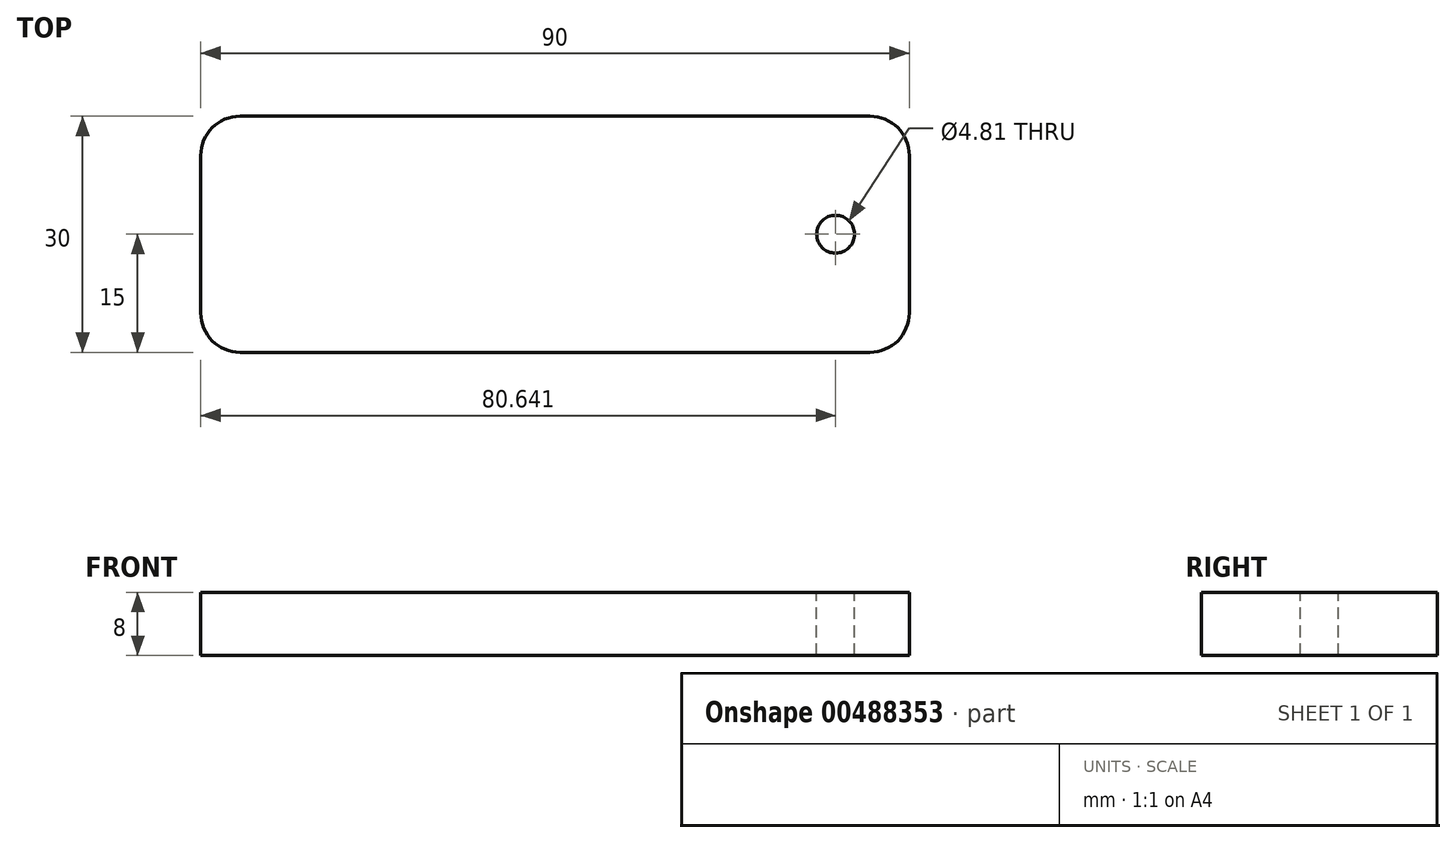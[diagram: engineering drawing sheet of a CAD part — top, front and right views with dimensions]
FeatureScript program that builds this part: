
annotation { "Feature Type Name" : "Feature", "Feature Type Description" : "" }
export const myFeature = defineFeature(function(context is Context, id is Id, definition is map)
    precondition{}
    {
        {
            var Q0;
            Q0=qCreatedBy(makeId("Top.planeOp"),FACE);
            var sketch = newSketch(context, id + "F0", { "sketchPlane" : qUnion([Q0])});
            skLineSegment(sketch, "E0.bottom", {"start": v(40, 15) * mm, "end": v(-40, 15) * mm});
            skLineSegment(sketch, "E0.top", {"start": v(40, -15) * mm, "end": v(-40, -15) * mm});
            skLineSegment(sketch, "E0.left", {"start": v(45, 10) * mm, "end": v(45, -10) * mm});
            skLineSegment(sketch, "E0.right", {"start": v(-45, 10) * mm, "end": v(-45, -10) * mm});
            skPoint(sketch, "E0.middle", {"position": v(0, 0) * mm});
            skPoint(sketch, "E1.visualSharp", {"position": v(-45, 15) * mm});
            skArc(sketch, "E1.filletArc", {"start": v(-40, 15) * mm, "mid": v(-43.54, 13.54) * mm, "end": v(-45, 10) * mm});
            skPoint(sketch, "E2.visualSharp", {"position": v(-45, -15) * mm});
            skArc(sketch, "E2.filletArc", {"start": v(-45, -10) * mm, "mid": v(-43.54, -13.54) * mm, "end": v(-40, -15) * mm});
            skPoint(sketch, "E3.visualSharp", {"position": v(45, 15) * mm});
            skArc(sketch, "E3.filletArc", {"start": v(45, 10) * mm, "mid": v(43.54, 13.54) * mm, "end": v(40, 15) * mm});
            skPoint(sketch, "E4.visualSharp", {"position": v(45, -15) * mm});
            skArc(sketch, "E4.filletArc", {"start": v(40, -15) * mm, "mid": v(43.54, -13.54) * mm, "end": v(45, -10) * mm});
            skSolve(sketch);
        }
        {
            var Q0;
            Q0 = qSketchRegion(id + "F0", true);
            extrude(context, id + "F1", {"entities" : qUnion([Q0]), "endBound" : BoundingType.SYMMETRIC, "depth" : 8 * mm});
        }
        {
            var Q0;
            Q0=makeQuery(id+"F1.opExtrude","CAP_FACE",FACE,{"disambiguationData":[OSD([sQuery(id+"F0.wireOp",EDGE,"E0.bottom"),sQuery(id+"F0.wireOp",EDGE,"E0.top"),sQuery(id+"F0.wireOp",EDGE,"E0.left"),sQuery(id+"F0.wireOp",EDGE,"E0.right"),sQuery(id+"F0.wireOp",EDGE,"E1.filletArc"),sQuery(id+"F0.wireOp",EDGE,"E2.filletArc"),sQuery(id+"F0.wireOp",EDGE,"E3.filletArc"),sQuery(id+"F0.wireOp",EDGE,"E4.filletArc")])],"isStart":false});
            var sketch = newSketch(context, id + "F2", { "sketchPlane" : qUnion([Q0])});
            skCircle(sketch, "E5", {"center": v(35.64, 0) * mm, "radius": 2.4 * mm});
            skSolve(sketch);
        }
        {
            var Q0;
            Q0 = qSketchRegion(id + "F2", true);
            extrude(context, id + "F3", {"entities" : qUnion([Q0]), "operationType" : NewBodyOperationType.REMOVE, "oppositeDirection" : true, "depth" : 11 * mm});
        }
    });
